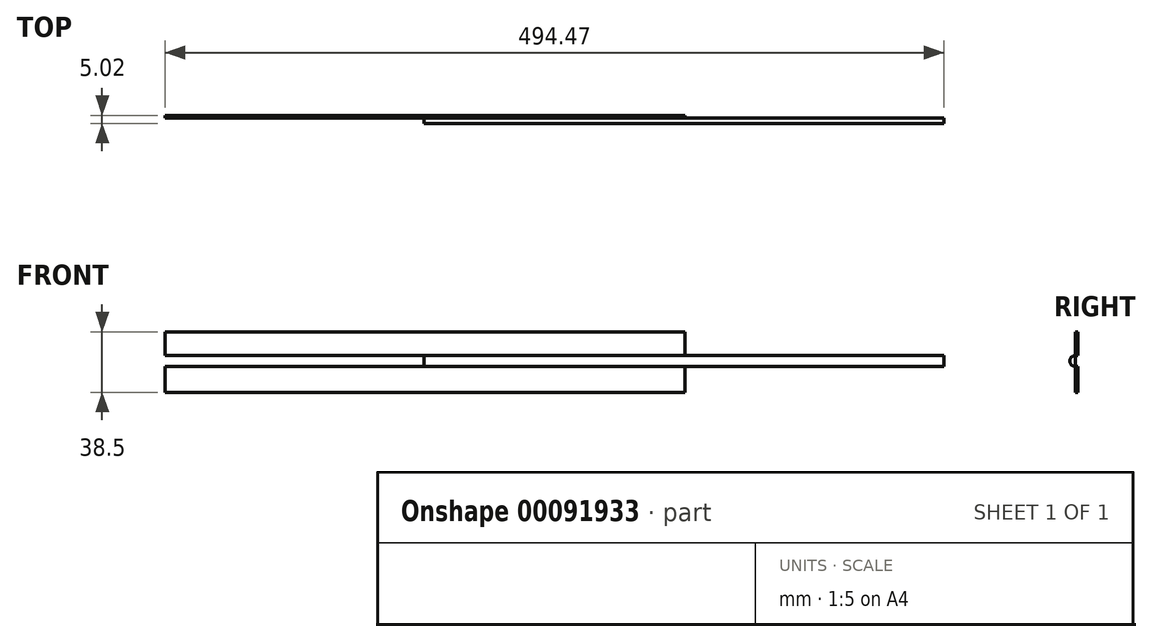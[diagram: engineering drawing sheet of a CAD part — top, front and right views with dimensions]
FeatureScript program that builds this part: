
annotation { "Feature Type Name" : "Feature", "Feature Type Description" : "" }
export const myFeature = defineFeature(function(context is Context, id is Id, definition is map)
    precondition{}
    {
        {
            var Q0;
            Q0=qCreatedBy(makeId("Front.planeOp"),FACE);
            var sketch = newSketch(context, id + "F0", { "sketchPlane" : qUnion([Q0])});
            skLineSegment(sketch, "E0.bottom", {"start": v(-164.27, -85.53) * mm, "end": v(165.93, -85.53) * mm});
            skLineSegment(sketch, "E0.left", {"start": v(-164.27, -85.53) * mm, "end": v(-164.27, -100.54) * mm});
            skLineSegment(sketch, "E0.right", {"start": v(165.93, -85.53) * mm, "end": v(165.93, -85.76) * mm});
            skLineSegment(sketch, "E1.bottom", {"start": v(-164.27, -107.52) * mm, "end": v(165.93, -107.52) * mm});
            skLineSegment(sketch, "E1.top", {"start": v(-164.27, -124.03) * mm, "end": v(165.93, -124.03) * mm});
            skLineSegment(sketch, "E1.left", {"start": v(-164.27, -107.52) * mm, "end": v(-164.27, -124.03) * mm});
            skLineSegment(sketch, "E1.right", {"start": v(165.93, -107.52) * mm, "end": v(165.93, -124.03) * mm});
            skLineSegment(sketch, "E2", {"start": v(-164.27, -107.52) * mm, "end": v(-164.27, -100.54) * mm, "construction": true});
            skLineSegment(sketch, "E3", {"start": v(-164.27, -100.54) * mm, "end": v(165.93, -100.54) * mm});
            skLineSegment(sketch, "E4", {"start": v(165.93, -100.54) * mm, "end": v(165.93, -107.52) * mm, "construction": true});
            skLineSegment(sketch, "E5", {"start": v(165.93, -100.54) * mm, "end": v(165.93, -85.76) * mm});
            skSolve(sketch);
        }
        {
            var Q0;
            Q0 = qSketchRegion(id + "F0", true);
            extrude(context, id + "F1", {"entities" : qUnion([Q0]), "depth" : 1.52 * mm});
        }
        {
            var Q0;
            Q0=qCreatedBy(makeId("Right.planeOp"),FACE);
            var sketch = newSketch(context, id + "F2", { "sketchPlane" : qUnion([Q0])});
            skLineSegment(sketch, "E6", {"start": v(-1.52, -100.54) * mm, "end": v(-1.52, -107.52) * mm});
            skArc(sketch, "E7", {"start": v(-5.02, -104.03) * mm, "mid": v(-4, -101.56) * mm, "end": v(-1.52, -100.54) * mm});
            skPoint(sketch, "E7.startSnap0", {"position": v(-1.52, -104.03) * mm});
            skLineSegment(sketch, "E8", {"start": v(-1.52, -104.03) * mm, "end": v(-5.02, -104.03) * mm, "construction": true});
            skArc(sketch, "E9.MirrorCS", {"start": v(-5.02, -104.03) * mm, "mid": v(-4, -106.5) * mm, "end": v(-1.52, -107.52) * mm});
            skSolve(sketch);
        }
        {
            var Q0;
            Q0 = qSketchRegion(id + "F2", true);
            extrude(context, id + "F3", {"entities" : qUnion([Q0]), "depth" : 330.2 * mm});
        }
    });
